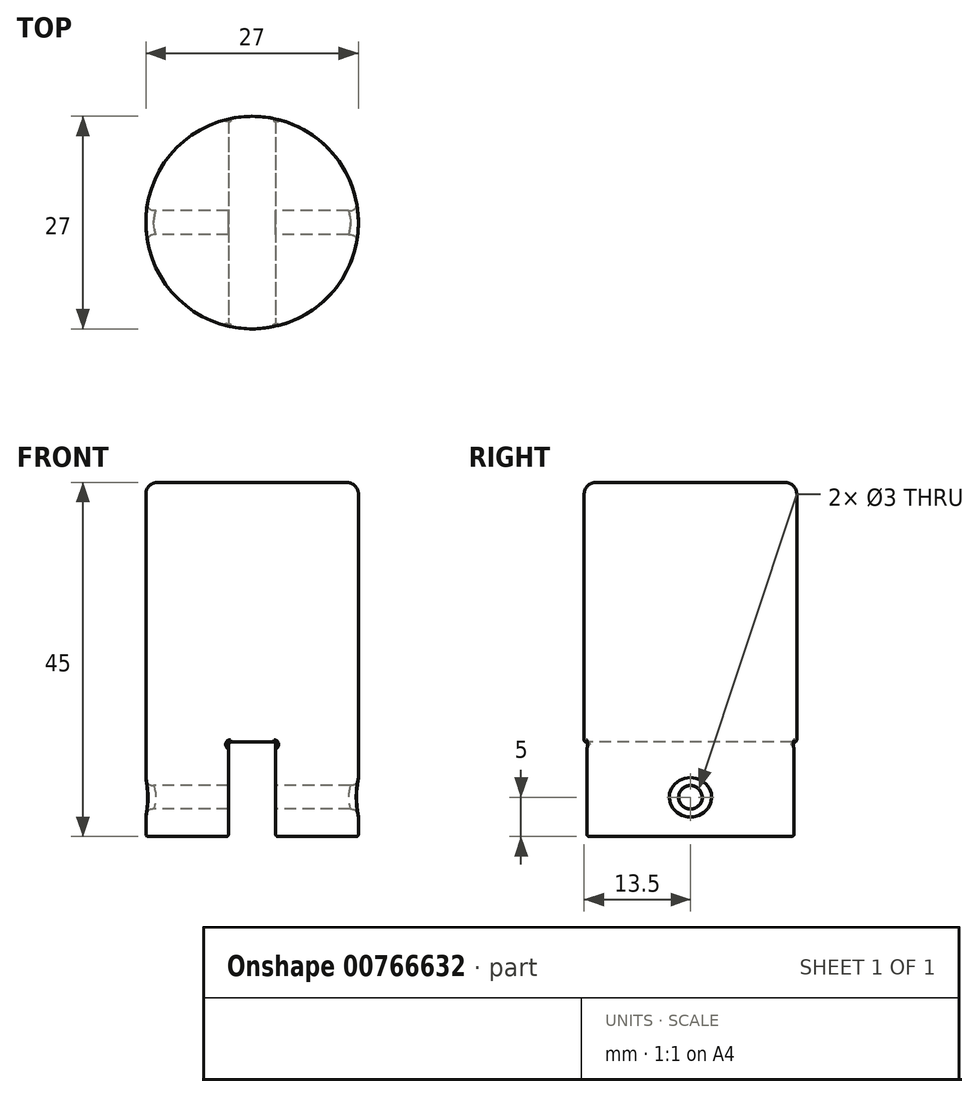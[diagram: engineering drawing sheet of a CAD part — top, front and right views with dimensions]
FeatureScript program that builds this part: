
annotation { "Feature Type Name" : "Feature", "Feature Type Description" : "" }
export const myFeature = defineFeature(function(context is Context, id is Id, definition is map)
    precondition{}
    {
        {
            var Q0;
            Q0=qCreatedBy(makeId("Top.planeOp"),FACE);
            var sketch = newSketch(context, id + "F0", { "sketchPlane" : qUnion([Q0])});
            skCircle(sketch, "E0", {"center": v(0, 0) * mm, "radius": 13.5 * mm});
            skLineSegment(sketch, "E1", {"start": v(-3, 13.16) * mm, "end": v(-3, -13.16) * mm});
            skLineSegment(sketch, "E2", {"start": v(3, 13.16) * mm, "end": v(3, -13.16) * mm});
            skSolve(sketch);
        }
        {
            var Q0;
            Q0 = qSketchRegion(id + "F0", true);
            extrude(context, id + "F1", {"entities" : qUnion([Q0]), "depth" : 33 * mm, "offsetDistance" : 25 * mm});
        }
        {
            var Q0;
            {var subQ0=sQuery(id+"F0.wireOp",EDGE,"E2");Q0=makeQuery(id+"F0.imprint","IMPRINT",FACE,{"disambiguationData":[TD([[makeQuery(id+"F0.imprint","IMPRINT",EDGE,{"derivedFrom":subQ0}),1.0]])]});}
            var Q1;
            {var subQ0=sQuery(id+"F0.wireOp",EDGE,"E1");Q1=makeQuery(id+"F0.imprint","IMPRINT",FACE,{"disambiguationData":[TD([[makeQuery(id+"F0.imprint","IMPRINT",EDGE,{"derivedFrom":subQ0}),-1.0]])]});}
            extrude(context, id + "F2", {"entities" : qUnion([Q0, Q1]), "operationType" : NewBodyOperationType.ADD, "depth" : -12 * mm, "offsetDistance" : 25 * mm});
        }
        {
            var Q0;
            Q0=makeQuery(id+"F1.opExtrude","CAP_FACE",FACE,{"disambiguationData":[OSD([sQuery(id+"F0.wireOp",EDGE,"E0")])],"isStart":false});
            fillet(context, id + "F3", {"entities" : qUnion([Q0]), "radius" : 1.5 * mm, "tangentPropagation" : true, "allowEdgeOverflow" : false});
        }
        {
            var Q0;
            Q0=qCreatedBy(makeId("Right.planeOp"),FACE);
            var sketch = newSketch(context, id + "F4", { "sketchPlane" : qUnion([Q0])});
            skCircle(sketch, "E3", {"center": v(0, -7) * mm, "radius": 1.5 * mm});
            skSolve(sketch);
        }
        {
            var Q0;
            Q0 = qSketchRegion(id + "F4", true);
            extrude(context, id + "F5", {"entities" : qUnion([Q0]), "operationType" : NewBodyOperationType.REMOVE, "endBound" : BoundingType.SYMMETRIC, "depth" : 55 * mm, "offsetDistance" : 25 * mm});
        }
        {
            var Q0;
            Q0=makeQuery(id+"F1.opExtrude","CAP_FACE",FACE,{"disambiguationData":[OSD([sQuery(id+"F0.wireOp",EDGE,"E0")])],"isStart":true});
            var Q1;
            Q1=makeQuery(id+"F2.opExtrude","CAP_FACE",FACE,{"disambiguationData":[OSD([sQuery(id+"F0.wireOp",EDGE,"E0"),sQuery(id+"F0.wireOp",EDGE,"E1")])],"isStart":false});
            var Q2;
            Q2=makeQuery(id+"F2.opExtrude","CAP_FACE",FACE,{"disambiguationData":[OSD([sQuery(id+"F0.wireOp",EDGE,"E0"),sQuery(id+"F0.wireOp",EDGE,"E2")])],"isStart":false});
            fillet(context, id + "F6", {"entities" : qUnion([Q0, Q1, Q2]), "radius" : .3 * mm, "tangentPropagation" : true, "allowEdgeOverflow" : false});
        }
        {
            var Q0;
            {var subQ0=sQuery(id+"F0.wireOp",EDGE,"E2");var subQ1=sQuery(id+"F0.wireOp",EDGE,"E0");var subQ2=sQuery(id+"F0.wireOp",EDGE,"E1");Q0=makeQuery(id+"F5.boolean.opBoolean","INTERSECT",EDGE,{"disambiguationData":[OD(0.0)],"derivedFrom":[makeQuery(id+"F2.boolean.opBoolean","MERGE",FACE,{"derivedFrom":[makeQuery(id+"F1.opExtrude","SWEPT_FACE",FACE,{"disambiguationData":[OSD([subQ1])]}),makeQuery(id+"F2.opExtrude","SWEPT_FACE",FACE,{"disambiguationData":[OSD([subQ1]),TDD([makeQuery(id+"F0.imprint","IMPRINT",EDGE,{"disambiguationData":[TD([[makeQuery(id+"F0.imprint","INTERSECT",VERTEX,{"disambiguationData":[OD(0.0)],"derivedFrom":[subQ1,subQ2]}),-1.0]])],"derivedFrom":subQ1})])]}),makeQuery(id+"F2.opExtrude","SWEPT_FACE",FACE,{"disambiguationData":[OSD([subQ1]),TDD([makeQuery(id+"F0.imprint","IMPRINT",EDGE,{"disambiguationData":[TD([[makeQuery(id+"F0.imprint","INTERSECT",VERTEX,{"disambiguationData":[OD(0.0)],"derivedFrom":[subQ1,subQ0]}),1.0]])],"derivedFrom":subQ1})])]})]}),makeQuery(id+"F5.opExtrude","SWEPT_FACE",FACE,{"disambiguationData":[OSD([sQuery(id+"F4.wireOp",EDGE,"E3")])]})]});}
            var Q1;
            {var subQ0=sQuery(id+"F0.wireOp",EDGE,"E2");var subQ1=sQuery(id+"F0.wireOp",EDGE,"E0");var subQ2=sQuery(id+"F0.wireOp",EDGE,"E1");Q1=makeQuery(id+"F5.boolean.opBoolean","INTERSECT",EDGE,{"disambiguationData":[OD(1.0)],"derivedFrom":[makeQuery(id+"F2.boolean.opBoolean","MERGE",FACE,{"derivedFrom":[makeQuery(id+"F1.opExtrude","SWEPT_FACE",FACE,{"disambiguationData":[OSD([subQ1])]}),makeQuery(id+"F2.opExtrude","SWEPT_FACE",FACE,{"disambiguationData":[OSD([subQ1]),TDD([makeQuery(id+"F0.imprint","IMPRINT",EDGE,{"disambiguationData":[TD([[makeQuery(id+"F0.imprint","INTERSECT",VERTEX,{"disambiguationData":[OD(0.0)],"derivedFrom":[subQ1,subQ2]}),-1.0]])],"derivedFrom":subQ1})])]}),makeQuery(id+"F2.opExtrude","SWEPT_FACE",FACE,{"disambiguationData":[OSD([subQ1]),TDD([makeQuery(id+"F0.imprint","IMPRINT",EDGE,{"disambiguationData":[TD([[makeQuery(id+"F0.imprint","INTERSECT",VERTEX,{"disambiguationData":[OD(0.0)],"derivedFrom":[subQ1,subQ0]}),1.0]])],"derivedFrom":subQ1})])]})]}),makeQuery(id+"F5.opExtrude","SWEPT_FACE",FACE,{"disambiguationData":[OSD([sQuery(id+"F4.wireOp",EDGE,"E3")])]})]});}
            fillet(context, id + "F7", {"entities" : qUnion([Q0, Q1]), "radius" : 1 * mm, "rho" : 0.5, "crossSection" : FilletCrossSection.CONIC, "allowEdgeOverflow" : false});
        }
    });
